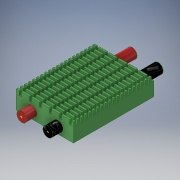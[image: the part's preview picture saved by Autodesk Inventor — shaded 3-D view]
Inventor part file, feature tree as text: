
AUTODESK INVENTOR PART (.ipt)
format: ipt  version: 2019.2 (Build 232265000, 265)  size: 870,400 bytes
history: native  units: mm
features: sketch x15, extrude x6, other x4, pattern_linear x2, emboss x2, projected_geometry x2, fillet x1
ambient origin geometry x8: Origin, YZ Plane, XZ Plane, XY Plane, X Axis, Y Axis, Z Axis, Center Point
bodies: Solid1 (feature_tree)
feature tree (32):
  extrude  "Extrusion1"  Depth=28.5mm
  sketch  "Sketch2"  dims[d2=9.1mm d3=0.0mm d4=1.0mm]
  extrude  "Extrusion2"  Depth=1.0mm
  pattern_linear  "Rectangular Pattern1"  Count1=6 Spacing1=5.0mm
  extrude  "Extrusion3"  Depth=2.0mm
  pattern_linear  "Rectangular Pattern2"  Spacing1=0.5mm  [1 undecoded]
  emboss  "Emboss1"
  extrude  "Extrusion4"  Depth=0.5mm
  extrude  "Extrusion5"  [1 undecoded]
  sketch  "Sketch7"  dims[d17=0.1mm d18=0.0mm]
  other  "OUT_NEGATIVE"
  sketch  "Sketch8"  dims[d19=5.0mm]
  other  "OUT_POSITIVE"
  sketch  "Sketch9"  dims[d20=6.5mm]
  other  "IN_POSITIVE"
  sketch  "Sketch10"  dims[d21=10.0mm d22=0.0mm]
  other  "IN_NEGATIVE"
  emboss  "Emboss2"
  extrude  "Extrusion6"  [1 undecoded]
  fillet  "Fillet1"  [1 undecoded]
  sketch  "Sketch13"  dims[d27=1.0mm]
  sketch  "Sketch14"  dims[d28=1.0mm]
  sketch  "Sketch15"  dims[d29=1.5mm d30=0.5mm d31=0.0mm d32=0.5mm]
  sketch  "Sketch1"  dims[d0=28.5mm d1=40.0mm]
  sketch  "Sketch3"  dims[d5=1.0mm]
  sketch  "Sketch4"  dims[d6=1.0mm]
  sketch  "Sketch5"  dims[d7=9.1mm d8=0.0mm d9=60.0mm d11=5.0mm]
  sketch  "Sketch6"  dims[d12=9.1mm d13=0.0mm d14=200.0mm d16=2.0mm]
  projected_geometry  "Projected Loop1"
  projected_geometry  "Projected Loop2"
  sketch  "Sketch11"  dims[d23=5.0mm d24=0.0mm]
  sketch  "Sketch12"  dims[d25=0.1mm d26=0.0mm]
note: 4 required parameter values undecoded (feature->parameter linkage not recoverable at this tier; creation-order binding heuristic only, values carry confidence <= 0.55)
